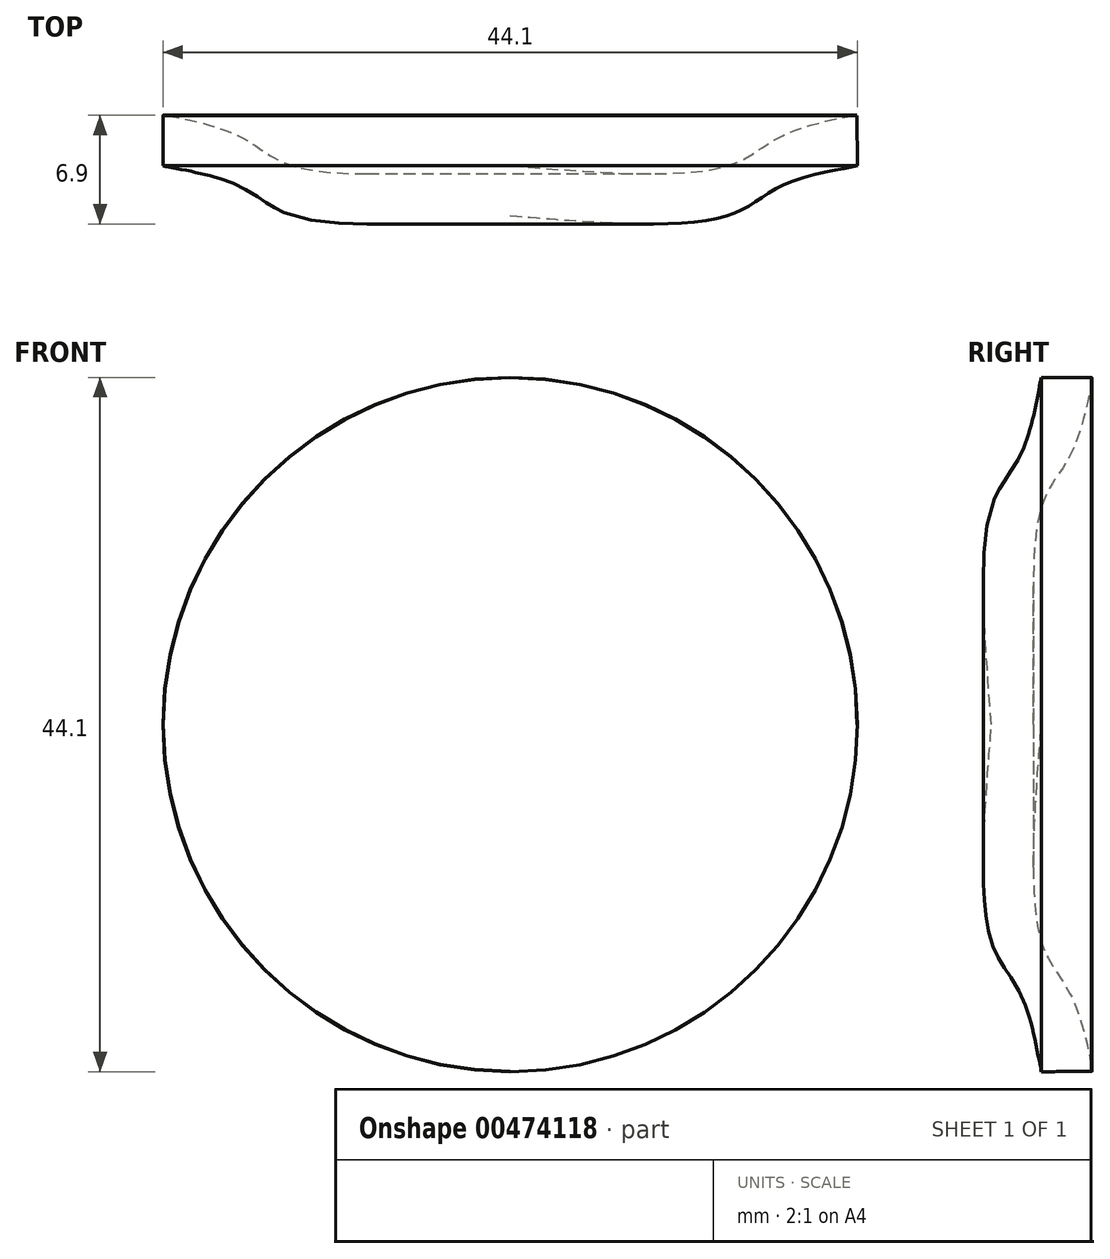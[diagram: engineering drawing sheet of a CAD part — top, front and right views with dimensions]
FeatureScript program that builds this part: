
annotation { "Feature Type Name" : "Feature", "Feature Type Description" : "" }
export const myFeature = defineFeature(function(context is Context, id is Id, definition is map)
    precondition{}
    {
        {
            var Q0;
            Q0=qCreatedBy(makeId("Top.planeOp"),FACE);
            var sketch = newSketch(context, id + "F0", { "sketchPlane" : qUnion([Q0])});
            skLineSegment(sketch, "E0", {"start": v(0, 0) * mm, "end": v(0, 3.18) * mm});
            skLineSegment(sketch, "E1", {"start": v(0, 0) * mm, "end": v(-9.13, 0) * mm});
            skFitSpline(sketch, "E2", {"points": [v(0, 3.17) * mm, v(13.85, 3.18) * mm, v(17.7, 5.28) * mm, v(22.05, 6.37) * mm, v(22.03, 6.35) * mm], "startDerivative": vector(36.24, -2.89) * mm, "endDerivative": vector(-1.79, -1.14) * mm});
            skFitSpline(sketch, "E3", {"points": [v(0, 0) * mm, v(13.85, 0) * mm, v(17.7, 2.1) * mm, v(22.05, 3.18) * mm, v(22.03, 3.17) * mm], "startDerivative": vector(36.24, -2.89) * mm, "endDerivative": vector(-1.79, -1.14) * mm});
            skLineSegment(sketch, "E4", {"start": v(22.03, 6.35) * mm, "end": v(22.05, 3.18) * mm});
            skSolve(sketch);
        }
        {
            var Q0;
            {var subQ0=sQuery(id+"F0.wireOp",EDGE,"E0");Q0=makeQuery(id+"F0.imprint","IMPRINT",FACE,{"disambiguationData":[TD([[makeQuery(id+"F0.imprint","IMPRINT",EDGE,{"derivedFrom":subQ0}),-1.0]])]});}
            var Q1;
            Q1=sQuery(id+"F0.wireOp",EDGE,"E0");
            revolve(context, id + "F1", {"entities" : qUnion([Q0]), "axis" : qUnion([Q1]), "revolveType" : RevolveType.SYMMETRIC, "angle" : 360 * degree});
        }
    });
